# Revit family: Toilet_Tissue_Seat_Dispenser_Napkin-Disposal-Bradley_Corp-Partition-Dual_Side-591
name_source: partatom
category: Specialty Equipment
revit_build: Autodesk Revit 2015 (Build: 20140223_1515(x64)
units: mm (PartAtom-declared; Revit-internal decimal feet)

## types (1)
- 591
    ADA Compliant = Yes
    Assembly Code = C1030200
    Buy American Act = Yes
    Cabinet Material = Metal - Bradley Corp - Stainless Steel Satin
    Default Elevation = 48"
    Depth = 4 1/2"
    Description = Combination Unit: 2 Stall Seat Cover, Tissue Dispenser & Napkin Disposal
    Fixed Flange Side Projection = 1 1/4"
    Flange Width = 1"
    Height = 30 5/8"
    Low Emitting Material = No
    Manufacturer = Bradley Corporation
    Manufacturer Revit Model URL = https://www.bradleycorp.com
    MasterFormat Number = 10 28 13. 13
    MasterFormat Title = Commercial Toilet Accessories
    Model = 591-000000
    OmniClass Code = 23.31.25.00
    OmniClass Title = Toilet and Bath Specialties
    Percentage of Recycled Content = 0
    Product Page URL = https://www.bradleycorp.com
    Product Tech Data URL - English = https://www.bradleycorp.com
    Specifications URL = https://www.bradleycorp.com
    URL = http://www.bradleycorp.com
    Version = 1.0
    Void Height = 28 7/8"
    Void Width = 15 3/8"
    Warranty Information = Complete unit, excepting mirrors warranted for one year.
    Width = 17 1/8"

## geometry (parser evidence)
native form markers: Blend x2, Sweep x1
no freeform markers — native parametric forms only
